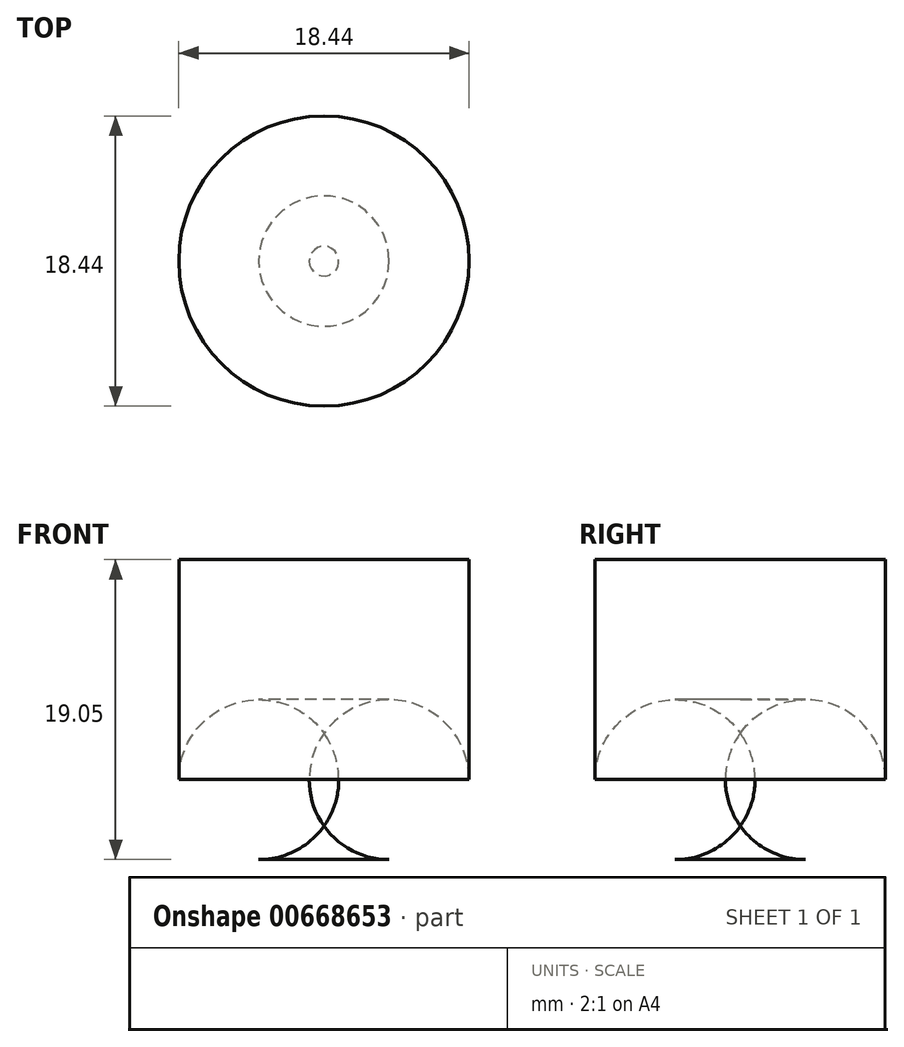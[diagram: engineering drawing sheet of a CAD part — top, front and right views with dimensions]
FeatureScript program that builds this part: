
annotation { "Feature Type Name" : "Feature", "Feature Type Description" : "" }
export const myFeature = defineFeature(function(context is Context, id is Id, definition is map)
    precondition{}
    {
        {
            var Q0;
            Q0=qCreatedBy(makeId("Top.planeOp"),FACE);
            var sketch = newSketch(context, id + "F0", { "sketchPlane" : qUnion([Q0])});
            skCircle(sketch, "E0", {"center": v(0, 0) * mm, "radius": 9.22 * mm});
            skSolve(sketch);
        }
        {
            var Q0;
            Q0=makeQuery(id+"F0.imprint","IMPRINT",FACE,{"disambiguationData":[TD([[makeQuery(id+"F0.imprint","IMPRINT",EDGE,{"derivedFrom":sQuery(id+"F0.wireOp",EDGE,"E0")}),1.0]])]});
            extrude(context, id + "F1", {"entities" : qUnion([Q0]), "depth" : 19.05 * mm, "offsetDistance" : 25.4 * mm});
        }
        {
            var Q0;
            Q0=qCreatedBy(makeId("Front.planeOp"),FACE);
            var sketch = newSketch(context, id + "F2", { "sketchPlane" : qUnion([Q0])});
            skLineSegment(sketch, "E1", {"start": v(0, 55.48) * mm, "end": v(0, 18.8) * mm});
            skSolve(sketch);
        }
        {
            var Q0;
            Q0=qCreatedBy(makeId("Right.planeOp"),FACE);
            var sketch = newSketch(context, id + "F3", { "sketchPlane" : qUnion([Q0])});
            skLineSegment(sketch, "E2", {"start": v(9.1, 18.92) * mm, "end": v(0, 55.57) * mm});
            skSolve(sketch);
        }
        {
            var Q0;
            Q0=sQuery(id+"F3.wireOp",EDGE,"E2");
            var Q1;
            Q1=sQuery(id+"F2.wireOp",EDGE,"E1");
            revolve(context, id + "F4", {"bodyType" : ToolBodyType.SURFACE, "surfaceEntities" : qUnion([Q0]), "axis" : qUnion([Q1]), "revolveType" : RevolveType.FULL});
        }
        {
            var Q0;
            Q0=makeQuery(id+"F1.opExtrude","CAP_EDGE",EDGE,{"disambiguationData":[OSD([sQuery(id+"F0.wireOp",EDGE,"E0")])],"isStart":true});
            fillet(context, id + "F5", {"entities" : qUnion([Q0]), "radius" : 5.08 * mm, "tangentPropagation" : true, "allowEdgeOverflow" : false});
        }
    });
